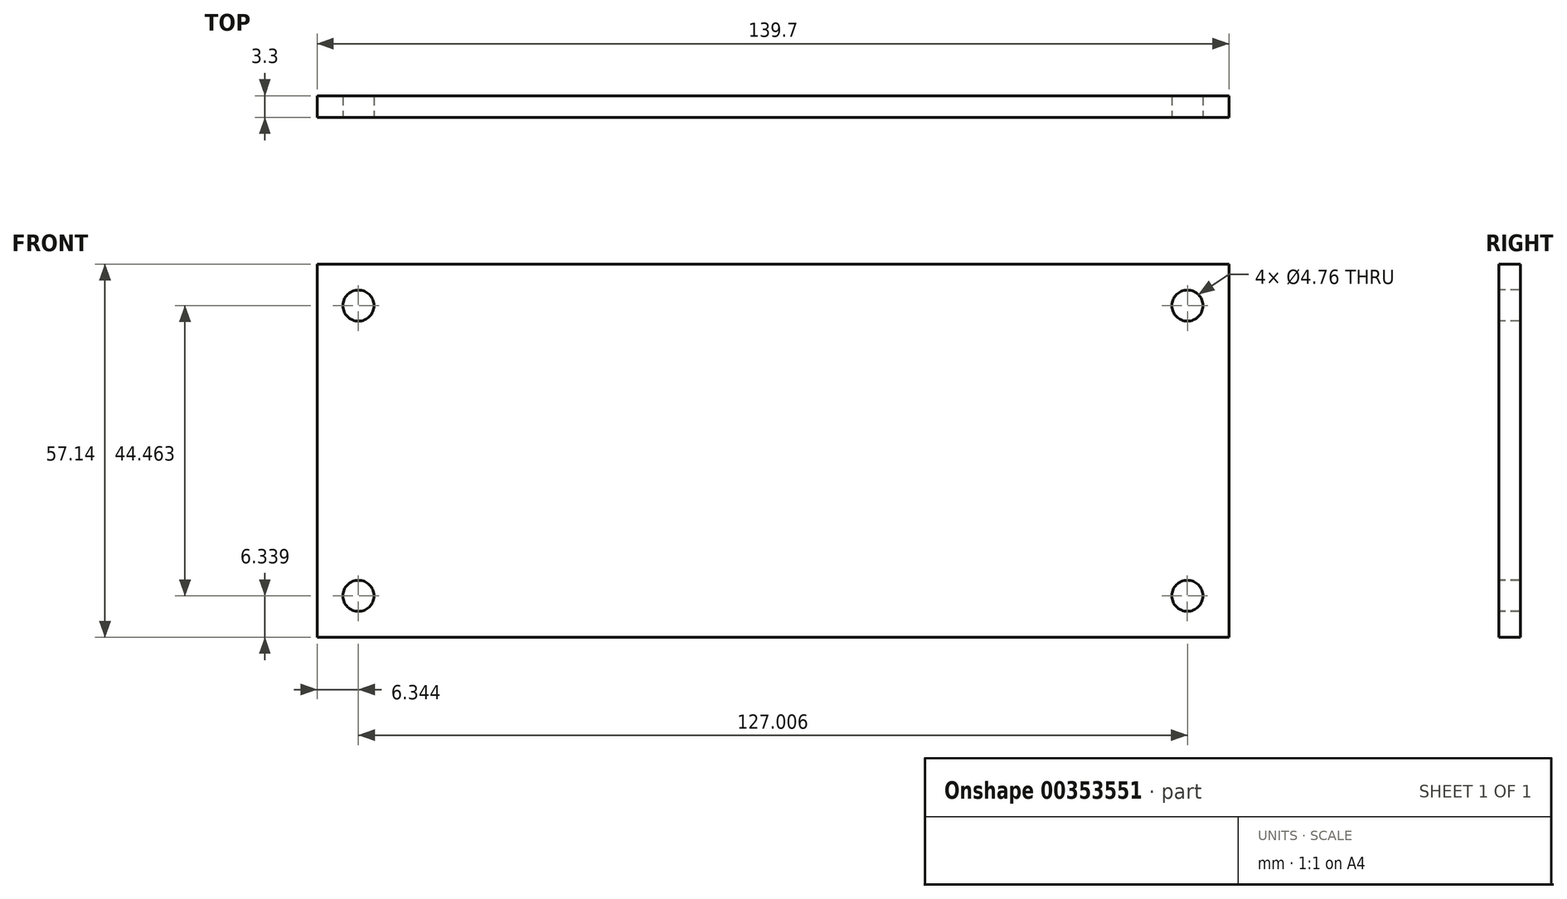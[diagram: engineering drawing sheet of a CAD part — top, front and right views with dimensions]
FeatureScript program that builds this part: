
annotation { "Feature Type Name" : "Feature", "Feature Type Description" : "" }
export const myFeature = defineFeature(function(context is Context, id is Id, definition is map)
    precondition{}
    {
        {
            var Q0;
            Q0=qCreatedBy(makeId("Front.planeOp"),FACE);
            var sketch = newSketch(context, id + "F0", { "sketchPlane" : qUnion([Q0])});
            skLineSegment(sketch, "E0.bottom", {"start": v(-69.85, 28.58) * mm, "end": v(69.85, 28.58) * mm});
            skLineSegment(sketch, "E0.top", {"start": v(-69.85, -28.57) * mm, "end": v(69.85, -28.57) * mm});
            skLineSegment(sketch, "E0.left", {"start": v(-69.85, 28.58) * mm, "end": v(-69.85, -28.57) * mm});
            skLineSegment(sketch, "E0.right", {"start": v(69.85, 28.58) * mm, "end": v(69.85, -28.57) * mm});
            skPoint(sketch, "E0.middle", {"position": v(0, 0) * mm});
            skSolve(sketch);
        }
        {
            var Q0;
            Q0 = qSketchRegion(id + "F0", true);
            extrude(context, id + "F1", {"entities" : qUnion([Q0]), "depth" : 3.3 * mm, "symmetric" : true});
        }
        {
            var Q0;
            Q0=makeQuery(id+"F1.opExtrude","CAP_FACE",FACE,{"disambiguationData":[OSD([sQuery(id+"F0.wireOp",EDGE,"E0.bottom"),sQuery(id+"F0.wireOp",EDGE,"E0.top"),sQuery(id+"F0.wireOp",EDGE,"E0.left"),sQuery(id+"F0.wireOp",EDGE,"E0.right")])],"isStart":false});
            var sketch = newSketch(context, id + "F2", { "sketchPlane" : qUnion([Q0])});
            skCircle(sketch, "E1", {"center": v(-63.5, 22.23) * mm, "radius": 2.38 * mm});
            skSolve(sketch);
        }
        {
            var Q0;
            Q0 = qSketchRegion(id + "F2", true);
            extrude(context, id + "F3", {"entities" : qUnion([Q0]), "operationType" : NewBodyOperationType.REMOVE, "endBound" : BoundingType.THROUGH_ALL, "oppositeDirection" : true, "depth" : 25.4 * mm});
        }
        {
            var Q0;
            Q0=makeQuery(id+"F1.opExtrude","CAP_FACE",FACE,{"disambiguationData":[OSD([sQuery(id+"F0.wireOp",EDGE,"E0.bottom"),sQuery(id+"F0.wireOp",EDGE,"E0.top"),sQuery(id+"F0.wireOp",EDGE,"E0.left"),sQuery(id+"F0.wireOp",EDGE,"E0.right")])],"isStart":false});
            var sketch = newSketch(context, id + "F4", { "sketchPlane" : qUnion([Q0])});
            skCircle(sketch, "E2", {"center": v(63.5, 22.23) * mm, "radius": 2.38 * mm});
            skSolve(sketch);
        }
        {
            var Q0;
            Q0 = qSketchRegion(id + "F4", true);
            extrude(context, id + "F5", {"entities" : qUnion([Q0]), "operationType" : NewBodyOperationType.REMOVE, "endBound" : BoundingType.THROUGH_ALL, "oppositeDirection" : true, "depth" : 25.4 * mm});
        }
        {
            var Q0;
            Q0=makeQuery(id+"F1.opExtrude","CAP_FACE",FACE,{"disambiguationData":[OSD([sQuery(id+"F0.wireOp",EDGE,"E0.bottom"),sQuery(id+"F0.wireOp",EDGE,"E0.top"),sQuery(id+"F0.wireOp",EDGE,"E0.left"),sQuery(id+"F0.wireOp",EDGE,"E0.right")])],"isStart":false});
            var sketch = newSketch(context, id + "F6", { "sketchPlane" : qUnion([Q0])});
            skCircle(sketch, "E3", {"center": v(-63.5, -22.23) * mm, "radius": 2.38 * mm});
            skSolve(sketch);
        }
        {
            var Q0;
            Q0 = qSketchRegion(id + "F6", true);
            extrude(context, id + "F7", {"entities" : qUnion([Q0]), "operationType" : NewBodyOperationType.REMOVE, "endBound" : BoundingType.THROUGH_ALL, "oppositeDirection" : true, "depth" : 25.4 * mm});
        }
        {
            var Q0;
            Q0=makeQuery(id+"F1.opExtrude","CAP_FACE",FACE,{"disambiguationData":[OSD([sQuery(id+"F0.wireOp",EDGE,"E0.bottom"),sQuery(id+"F0.wireOp",EDGE,"E0.top"),sQuery(id+"F0.wireOp",EDGE,"E0.left"),sQuery(id+"F0.wireOp",EDGE,"E0.right")])],"isStart":false});
            var sketch = newSketch(context, id + "F8", { "sketchPlane" : qUnion([Q0])});
            skCircle(sketch, "E4", {"center": v(63.5, -22.22) * mm, "radius": 2.38 * mm});
            skSolve(sketch);
        }
        {
            var Q0;
            Q0 = qSketchRegion(id + "F8", true);
            extrude(context, id + "F9", {"entities" : qUnion([Q0]), "operationType" : NewBodyOperationType.REMOVE, "endBound" : BoundingType.THROUGH_ALL, "oppositeDirection" : true, "depth" : 25.4 * mm});
        }
    });
